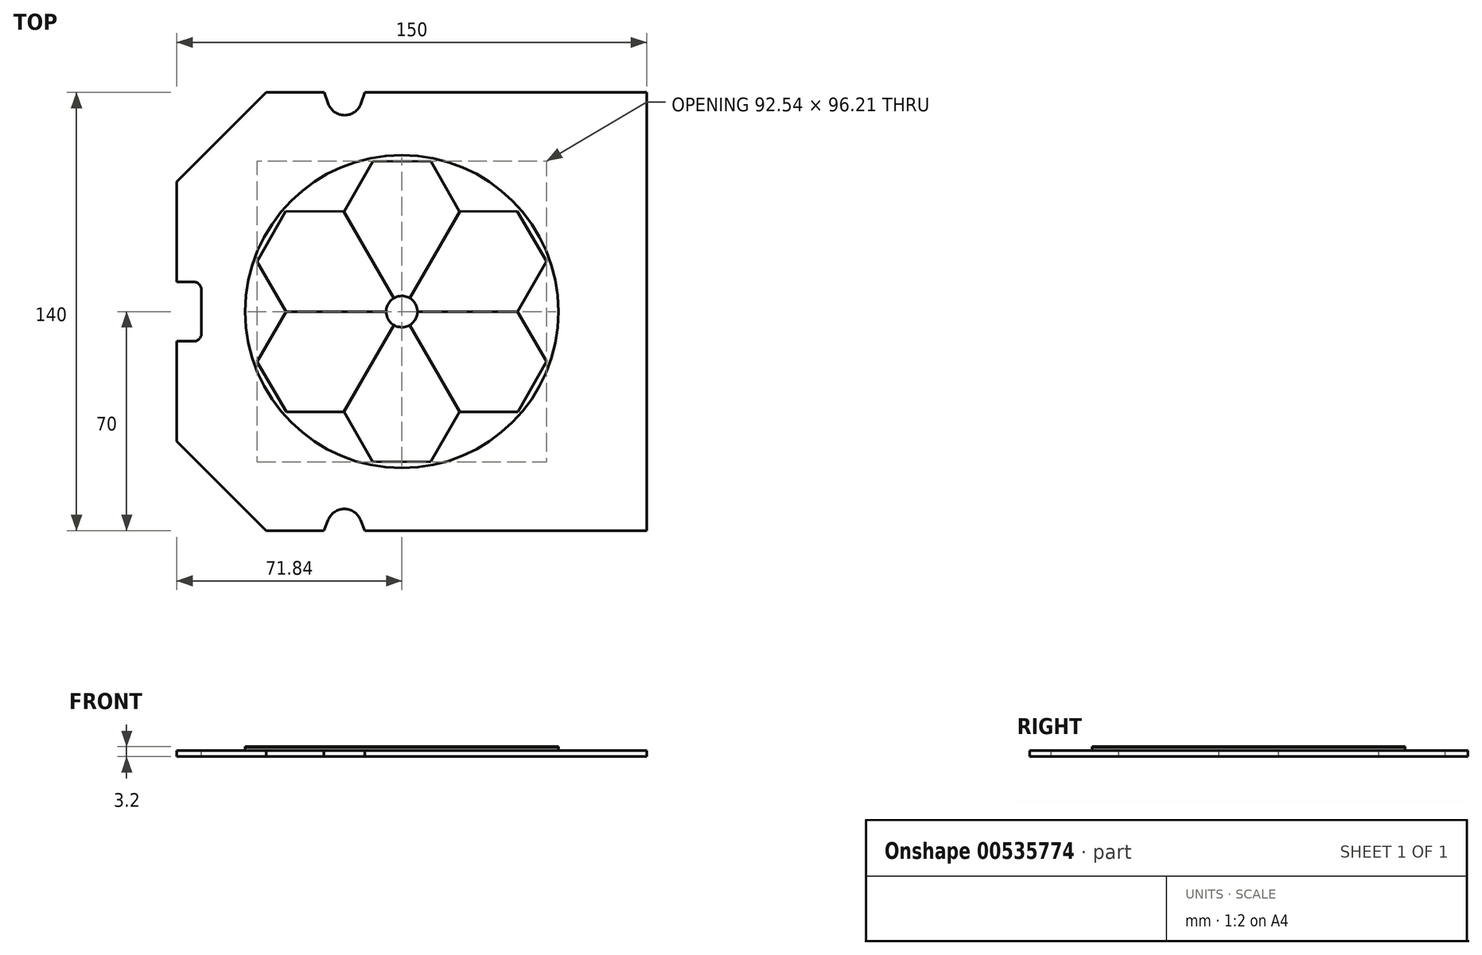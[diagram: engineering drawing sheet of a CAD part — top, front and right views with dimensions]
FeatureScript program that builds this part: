
annotation { "Feature Type Name" : "Feature", "Feature Type Description" : "" }
export const myFeature = defineFeature(function(context is Context, id is Id, definition is map)
    precondition{}
    {
        {
            var Q0;
            Q0=qCreatedBy(makeId("Top.planeOp"),FACE);
            var sketch = newSketch(context, id + "F0", { "sketchPlane" : qUnion([Q0])});
            skLineSegment(sketch, "E0.bottom", {"start": v(75, -70) * mm, "end": v(-75, -70) * mm});
            skLineSegment(sketch, "E0.top", {"start": v(75, 70) * mm, "end": v(-75, 70) * mm});
            skLineSegment(sketch, "E0.left", {"start": v(75, -70) * mm, "end": v(75, 70) * mm});
            skLineSegment(sketch, "E0.right", {"start": v(-75, -70) * mm, "end": v(-75, 70) * mm});
            skPoint(sketch, "E0.middle", {"position": v(0, 0) * mm});
            skSolve(sketch);
        }
        {
            var Q0;
            Q0=qSketchRegion(id+"F0",true);
            extrude(context, id + "F1", {"entities" : qUnion([Q0]), "depth" : 2 * mm, "offsetDistance" : 25 * mm});
        }
        {
            var Q0;
            Q0=makeQuery(id+"F1.opExtrude","CAP_FACE",FACE,{"disambiguationData":[OSD([sQuery(id+"F0.wireOp",EDGE,"E0.bottom"),sQuery(id+"F0.wireOp",EDGE,"E0.top"),sQuery(id+"F0.wireOp",EDGE,"E0.left"),sQuery(id+"F0.wireOp",EDGE,"E0.right")])],"isStart":false});
            var sketch = newSketch(context, id + "F2", { "sketchPlane" : qUnion([Q0])});
            skLineSegment(sketch, "E1", {"start": v(-75, 41.5) * mm, "end": v(-46.5, 70) * mm});
            skLineSegment(sketch, "E2", {"start": v(-75, -41.5) * mm, "end": v(-46.5, -70) * mm});
            skSolve(sketch);
        }
        {
            var Q0;
            Q0=qSketchRegion(id+"F2",true);
            var Q1;
            {var subQ0=sQuery(id+"F2.wireOp",EDGE,"E1");Q1=makeQuery(id+"F2.imprint","IMPRINT",FACE,{"disambiguationData":[TD([[makeQuery(id+"F2.imprint","IMPRINT",EDGE,{"derivedFrom":subQ0}),1.0]])]});}
            var Q2;
            {var subQ0=sQuery(id+"F2.wireOp",EDGE,"E2");Q2=makeQuery(id+"F2.imprint","IMPRINT",FACE,{"disambiguationData":[TD([[makeQuery(id+"F2.imprint","IMPRINT",EDGE,{"derivedFrom":subQ0}),-1.0]])]});}
            extrude(context, id + "F3", {"entities" : qUnion([Q0, Q1, Q2]), "operationType" : NewBodyOperationType.REMOVE, "endBound" : BoundingType.THROUGH_ALL, "oppositeDirection" : true, "depth" : 25 * mm, "offsetDistance" : 25 * mm});
        }
        {
            var Q0;
            Q0=makeQuery(id+"F1.opExtrude","CAP_FACE",FACE,{"disambiguationData":[OSD([sQuery(id+"F0.wireOp",EDGE,"E0.bottom"),sQuery(id+"F0.wireOp",EDGE,"E0.top"),sQuery(id+"F0.wireOp",EDGE,"E0.left"),sQuery(id+"F0.wireOp",EDGE,"E0.right")])],"isStart":false});
            var sketch = newSketch(context, id + "F4", { "sketchPlane" : qUnion([Q0])});
            skLineSegment(sketch, "E3", {"start": v(-75, 9.5) * mm, "end": v(-69.68, 9.5) * mm});
            skLineSegment(sketch, "E4", {"start": v(-67.18, 7) * mm, "end": v(-67.18, -7) * mm});
            skArc(sketch, "E5", {"start": v(-67.18, 7) * mm, "mid": v(-67.91, 8.77) * mm, "end": v(-69.68, 9.5) * mm});
            skLineSegment(sketch, "E6", {"start": v(-75, -9.5) * mm, "end": v(-69.68, -9.5) * mm});
            skArc(sketch, "E7", {"start": v(-69.68, -9.5) * mm, "mid": v(-67.91, -8.77) * mm, "end": v(-67.18, -7) * mm});
            skSolve(sketch);
        }
        {
            var Q0;
            Q0=qSketchRegion(id+"F4",true);
            var Q1;
            {var subQ1=sQuery(id+"F4.wireOp",EDGE,"E3");Q1=makeQuery(id+"F4.imprint","IMPRINT",FACE,{"disambiguationData":[TD([[makeQuery(id+"F4.imprint","IMPRINT",EDGE,{"derivedFrom":subQ1}),-1.0]])]});}
            extrude(context, id + "F5", {"entities" : qUnion([Q0, Q1]), "operationType" : NewBodyOperationType.REMOVE, "endBound" : BoundingType.THROUGH_ALL, "oppositeDirection" : true, "depth" : 25 * mm, "offsetDistance" : 25 * mm});
        }
        {
            var Q0;
            Q0=makeQuery(id+"F1.opExtrude","CAP_FACE",FACE,{"disambiguationData":[OSD([sQuery(id+"F0.wireOp",EDGE,"E0.bottom"),sQuery(id+"F0.wireOp",EDGE,"E0.top"),sQuery(id+"F0.wireOp",EDGE,"E0.left"),sQuery(id+"F0.wireOp",EDGE,"E0.right")])],"isStart":false});
            var sketch = newSketch(context, id + "F6", { "sketchPlane" : qUnion([Q0])});
            skArc(sketch, "E8", {"start": v(-26.63, 66.43) * mm, "mid": v(-21.44, 62.74) * mm, "end": v(-16.24, 66.43) * mm});
            skArc(sketch, "E9", {"start": v(-16.42, -66.5) * mm, "mid": v(-21.52, -63.06) * mm, "end": v(-26.61, -66.5) * mm});
            skLineSegment(sketch, "E10", {"start": v(-27.88, 70) * mm, "end": v(-26.63, 66.43) * mm});
            skLineSegment(sketch, "E11", {"start": v(-15, 70) * mm, "end": v(-16.24, 66.43) * mm});
            skLineSegment(sketch, "E12", {"start": v(-26.61, -66.5) * mm, "end": v(-28.03, -70) * mm});
            skLineSegment(sketch, "E13", {"start": v(-16.42, -66.5) * mm, "end": v(-15, -70) * mm});
            skSolve(sketch);
        }
        {
            var Q0;
            Q0=qSketchRegion(id+"F6",true);
            var Q1;
            Q1=makeQuery(id+"F6.imprint","IMPRINT",FACE,{"disambiguationData":[TD([[makeQuery(id+"F6.imprint","IMPRINT",EDGE,{"derivedFrom":sQuery(id+"F6.wireOp",EDGE,"E9")}),1.0]])]});
            var Q2;
            Q2=makeQuery(id+"F6.imprint","IMPRINT",FACE,{"disambiguationData":[TD([[makeQuery(id+"F6.imprint","IMPRINT",EDGE,{"derivedFrom":sQuery(id+"F6.wireOp",EDGE,"E8")}),1.0]])]});
            extrude(context, id + "F7", {"entities" : qUnion([Q0, Q1, Q2]), "operationType" : NewBodyOperationType.REMOVE, "endBound" : BoundingType.THROUGH_ALL, "oppositeDirection" : true, "depth" : 25 * mm, "offsetDistance" : 25 * mm});
        }
        {
            var Q0;
            Q0=makeQuery(id+"F1.opExtrude","CAP_FACE",FACE,{"disambiguationData":[OSD([sQuery(id+"F0.wireOp",EDGE,"E0.bottom"),sQuery(id+"F0.wireOp",EDGE,"E0.top"),sQuery(id+"F0.wireOp",EDGE,"E0.left"),sQuery(id+"F0.wireOp",EDGE,"E0.right")])],"isStart":false});
            var sketch = newSketch(context, id + "F8", { "sketchPlane" : qUnion([Q0])});
            skCircle(sketch, "E14", {"center": v(-3.16, 0) * mm, "radius": 50 * mm});
            skPoint(sketch, "E14.first.point", {"position": v(-36.36, 37.39) * mm});
            skPoint(sketch, "E14.second.point", {"position": v(32.35, -35.2) * mm});
            skPoint(sketch, "E14.third.point", {"position": v(42.82, 19.64) * mm});
            skSolve(sketch);
        }
        {
            var Q0;
            Q0=qSketchRegion(id+"F8",true);
            extrude(context, id + "F9", {"entities" : qUnion([Q0]), "operationType" : NewBodyOperationType.ADD, "depth" : 1 * mm, "offsetDistance" : 25 * mm});
        }
        {
            var Q0;
            Q0=makeQuery(id+"F9.opExtrude","CAP_FACE",FACE,{"disambiguationData":[OSD([sQuery(id+"F8.wireOp",EDGE,"E14")])],"isStart":false});
            var sketch = newSketch(context, id + "F10", { "sketchPlane" : qUnion([Q0])});
            skCircle(sketch, "E15", {"center": v(-3.16, 0) * mm, "radius": 5 * mm});
            skLineSegment(sketch, "E16", {"start": v(-3.16, 0) * mm, "end": v(-3.16, 32.02) * mm, "construction": true});
            skCircle(sketch, "E17", {"center": v(-3.16, 32.02) * mm, "radius": 16 * mm, "construction": true});
            skLineSegment(sketch, "E18", {"start": v(-12.47, 47.94) * mm, "end": v(6.06, 48.1) * mm});
            skLineSegment(sketch, "E19", {"start": v(6.06, 48.1) * mm, "end": v(15.3, 32) * mm});
            skLineSegment(sketch, "E20", {"start": v(-12.47, 47.94) * mm, "end": v(-21.62, 32) * mm});
            skLineSegment(sketch, "E21", {"start": v(-21.62, 32) * mm, "end": v(-5.66, 4.33) * mm});
            skLineSegment(sketch, "E22", {"start": v(15.3, 32) * mm, "end": v(-0.66, 4.33) * mm});
            skPoint(sketch, "E23.center", {"position": v(0, 0) * mm});
            skLineSegment(sketch, "E24.1.1", {"start": v(15.33, 32) * mm, "end": v(-0.66, 4.33) * mm});
            skLineSegment(sketch, "E25.1.0", {"start": v(-21.65, 32) * mm, "end": v(-5.66, 4.33) * mm});
            skLineSegment(sketch, "E25.2.1", {"start": v(6.14, 47.96) * mm, "end": v(15.3, 32) * mm});
            skLineSegment(sketch, "E25.2.2", {"start": v(-12.39, 47.8) * mm, "end": v(6.14, 47.96) * mm});
            skLineSegment(sketch, "E25.2.3", {"start": v(-12.39, 47.8) * mm, "end": v(-21.54, 31.87) * mm});
            skLineSegment(sketch, "E25.2.4", {"start": v(-21.57, 31.85) * mm, "end": v(-5.58, 4.2) * mm});
            skLineSegment(sketch, "E26.1.1", {"start": v(-40.21, 32.03) * mm, "end": v(-21.65, 32) * mm});
            skLineSegment(sketch, "E26.1.2", {"start": v(-49.33, 15.9) * mm, "end": v(-40.21, 32.03) * mm});
            skLineSegment(sketch, "E26.1.3", {"start": v(-49.33, 15.9) * mm, "end": v(-40.1, 0.02) * mm});
            skLineSegment(sketch, "E26.1.4", {"start": v(-40.1, -0.02) * mm, "end": v(-8.16, 0) * mm});
            skLineSegment(sketch, "E26.2.0", {"start": v(-40.1, 0.02) * mm, "end": v(-8.16, 0) * mm});
            skLineSegment(sketch, "E26.2.1", {"start": v(-49.43, -16.07) * mm, "end": v(-40.1, -0.02) * mm});
            skLineSegment(sketch, "E26.2.2", {"start": v(-40.03, -32.03) * mm, "end": v(-49.43, -16.07) * mm});
            skLineSegment(sketch, "E26.2.3", {"start": v(-40.03, -32.03) * mm, "end": v(-21.65, -32) * mm});
            skLineSegment(sketch, "E26.2.4", {"start": v(-21.62, -32) * mm, "end": v(-5.66, -4.33) * mm});
            skLineSegment(sketch, "E26.3.0", {"start": v(-21.65, -32) * mm, "end": v(-5.66, -4.33) * mm});
            skLineSegment(sketch, "E26.3.1", {"start": v(-12.38, -48.1) * mm, "end": v(-21.62, -32) * mm});
            skLineSegment(sketch, "E26.3.2", {"start": v(6.15, -47.94) * mm, "end": v(-12.38, -48.1) * mm});
            skLineSegment(sketch, "E26.3.3", {"start": v(6.15, -47.94) * mm, "end": v(15.3, -32) * mm});
            skLineSegment(sketch, "E26.3.4", {"start": v(15.33, -32) * mm, "end": v(-0.66, -4.33) * mm});
            skLineSegment(sketch, "E26.4.0", {"start": v(15.3, -32) * mm, "end": v(-0.66, -4.33) * mm});
            skLineSegment(sketch, "E26.4.1", {"start": v(33.9, -32.03) * mm, "end": v(15.33, -32) * mm});
            skLineSegment(sketch, "E26.4.2", {"start": v(43.01, -15.9) * mm, "end": v(33.9, -32.03) * mm});
            skLineSegment(sketch, "E26.4.3", {"start": v(43.01, -15.9) * mm, "end": v(33.79, -0.02) * mm});
            skLineSegment(sketch, "E26.4.4", {"start": v(33.79, 0.02) * mm, "end": v(1.84, 0) * mm});
            skLineSegment(sketch, "E26.5.0", {"start": v(33.79, -0.02) * mm, "end": v(1.84, 0) * mm});
            skLineSegment(sketch, "E26.5.1", {"start": v(43.1, 16.07) * mm, "end": v(33.79, 0.02) * mm});
            skLineSegment(sketch, "E26.5.2", {"start": v(33.7, 32.03) * mm, "end": v(43.1, 16.07) * mm});
            skLineSegment(sketch, "E26.5.3", {"start": v(33.7, 32.03) * mm, "end": v(15.33, 32) * mm});
            skSolve(sketch);
        }
        {
            var Q0;
            Q0=makeQuery(id+"F10.imprint","IMPRINT",FACE,{"disambiguationData":[TD([[makeQuery(id+"F10.imprint","IMPRINT",EDGE,{"derivedFrom":sQuery(id+"F10.wireOp",EDGE,"E24.1.1")}),-1.0]])]});
            var Q1;
            {var subQ0=sQuery(id+"F10.wireOp",EDGE,"E15");var subQ4=makeQuery(id+"F10.imprint","INTERSECT",VERTEX,{"derivedFrom":[subQ0,sQuery(id+"F10.wireOp",EDGE,"E24.1.1"),sQuery(id+"F10.wireOp",EDGE,"E22")]});Q1=makeQuery(id+"F10.imprint","IMPRINT",FACE,{"disambiguationData":[TD([[makeQuery(id+"F10.imprint","IMPRINT",EDGE,{"disambiguationData":[TD([[subQ4,1.0]])],"derivedFrom":subQ0}),1.0]])]});}
            extrude(context, id + "F11", {"entities" : qUnion([Q0, Q1]), "depth" : 0.2 * mm, "offsetDistance" : 25 * mm});
        }
    });
